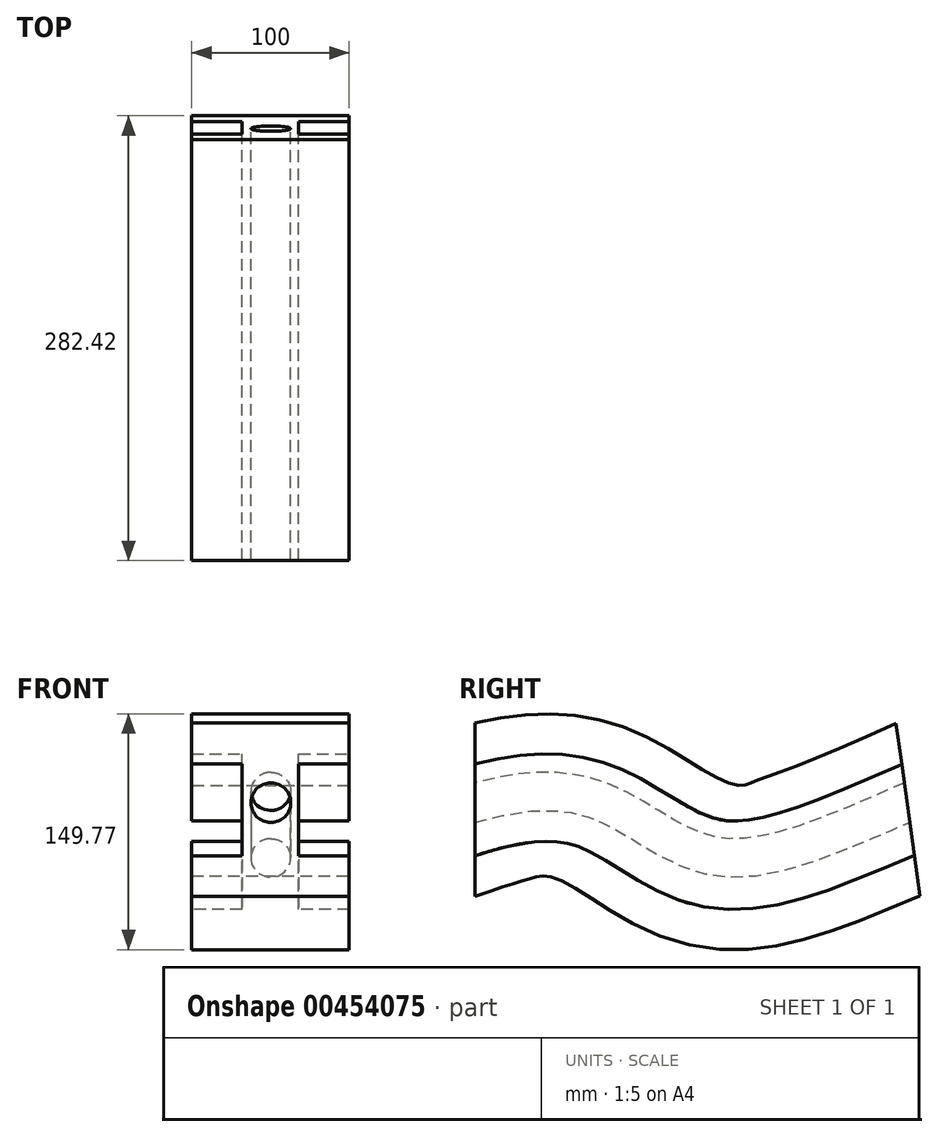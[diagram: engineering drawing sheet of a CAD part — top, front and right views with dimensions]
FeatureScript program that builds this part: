
annotation { "Feature Type Name" : "Feature", "Feature Type Description" : "" }
export const myFeature = defineFeature(function(context is Context, id is Id, definition is map)
    precondition{}
    {
        {
            var Q0;
            Q0=qCreatedBy(makeId("Front.planeOp"),FACE);
            var sketch = newSketch(context, id + "F0", { "sketchPlane" : qUnion([Q0])});
            skLineSegment(sketch, "E0", {"start": v(-50.93, 47.86) * mm, "end": v(49.07, 47.86) * mm});
            skLineSegment(sketch, "E1", {"start": v(49.07, 47.86) * mm, "end": v(49.07, 21.86) * mm});
            skLineSegment(sketch, "E2", {"start": v(49.07, 21.86) * mm, "end": v(17.07, 21.86) * mm});
            skLineSegment(sketch, "E3", {"start": v(17.07, 21.86) * mm, "end": v(17.07, -36.48) * mm});
            skLineSegment(sketch, "E4", {"start": v(17.07, -36.48) * mm, "end": v(49.07, -36.48) * mm});
            skLineSegment(sketch, "E5", {"start": v(49.07, -36.48) * mm, "end": v(49.07, -62.48) * mm});
            skLineSegment(sketch, "E6", {"start": v(49.07, -62.48) * mm, "end": v(-50.93, -62.48) * mm});
            skLineSegment(sketch, "E7", {"start": v(-50.93, -62.48) * mm, "end": v(-50.93, -36.48) * mm});
            skLineSegment(sketch, "E8", {"start": v(-50.93, -36.48) * mm, "end": v(-18.93, -36.48) * mm});
            skPoint(sketch, "E8.endSnap0", {"position": v(33.07, -36.48) * mm});
            skLineSegment(sketch, "E9", {"start": v(-18.93, -36.48) * mm, "end": v(-18.93, 21.86) * mm});
            skLineSegment(sketch, "E10", {"start": v(-18.93, 21.86) * mm, "end": v(-50.93, 21.86) * mm});
            skLineSegment(sketch, "E11", {"start": v(-50.93, 21.86) * mm, "end": v(-50.93, 47.86) * mm});
            skSolve(sketch);
        }
        {
            var Q0;
            Q0=qCreatedBy(makeId("Right.planeOp"),FACE);
            var sketch = newSketch(context, id + "F1", { "sketchPlane" : qUnion([Q0])});
            skFitSpline(sketch, "E12", {"points": [v(0, 0) * mm, v(82.07, 0) * mm, v(147.4, -32.98) * mm, v(273.91, 0) * mm], "startDerivative": vector(311.07, 87.62) * mm, "endDerivative": vector(466.85, 203.59) * mm});
            skSolve(sketch);
        }
        {
            var Q0;
            Q0=makeQuery(id+"F0.imprint","IMPRINT",FACE,{"disambiguationData":[TD([[makeQuery(id+"F0.imprint","IMPRINT",EDGE,{"derivedFrom":sQuery(id+"F0.wireOp",EDGE,"E0")}),-1.0]])]});
            var Q1;
            Q1=sQuery(id+"F1.wireOp",EDGE,"E12");
            sweep(context, id + "F2", {"profiles" : qUnion([Q0]), "path" : qUnion([Q1])});
        }
        {
            var Q0;
            Q0=makeQuery(id+"F2.opSweep","CAP_FACE",FACE,{"disambiguationData":[OSD([sQuery(id+"F0.wireOp",EDGE,"E0"),sQuery(id+"F0.wireOp",EDGE,"E1"),sQuery(id+"F0.wireOp",EDGE,"E2"),sQuery(id+"F0.wireOp",EDGE,"E3"),sQuery(id+"F0.wireOp",EDGE,"E4"),sQuery(id+"F0.wireOp",EDGE,"E5"),sQuery(id+"F0.wireOp",EDGE,"E6"),sQuery(id+"F0.wireOp",EDGE,"E7"),sQuery(id+"F0.wireOp",EDGE,"E8"),sQuery(id+"F0.wireOp",EDGE,"E9"),sQuery(id+"F0.wireOp",EDGE,"E10"),sQuery(id+"F0.wireOp",EDGE,"E11"),sQuery(id+"F1.wireOp",VERTEX,"E12.end")])],"isStart":false});
            var sketch = newSketch(context, id + "F3", { "sketchPlane" : qUnion([Q0])});
            skCircle(sketch, "E13", {"center": v(0.66, -40.13) * mm, "radius": 12.62 * mm});
            skPoint(sketch, "E13.first.point", {"position": v(0, -27.53) * mm});
            skPoint(sketch, "E13.second.point", {"position": v(0, -52.73) * mm});
            skPoint(sketch, "E13.third.point", {"position": v(13.24, -39.3) * mm});
            skSolve(sketch);
        }
        {
            var Q0;
            Q0=makeQuery(id+"F3.imprint","IMPRINT",FACE,{"disambiguationData":[TD([[makeQuery(id+"F3.imprint","IMPRINT",EDGE,{"derivedFrom":sQuery(id+"F3.wireOp",EDGE,"E13")}),1.0]])]});
            var Q1;
            Q1 = qConstructionFilter(qBodyType(qCreatedBy(id + "F1" ,EDGE), BodyType.WIRE), ConstructionObject.NO);
            sweep(context, id + "F4", {"operationType" : NewBodyOperationType.REMOVE, "profiles" : qUnion([Q0]), "path" : qUnion([Q1])});
        }
    });
